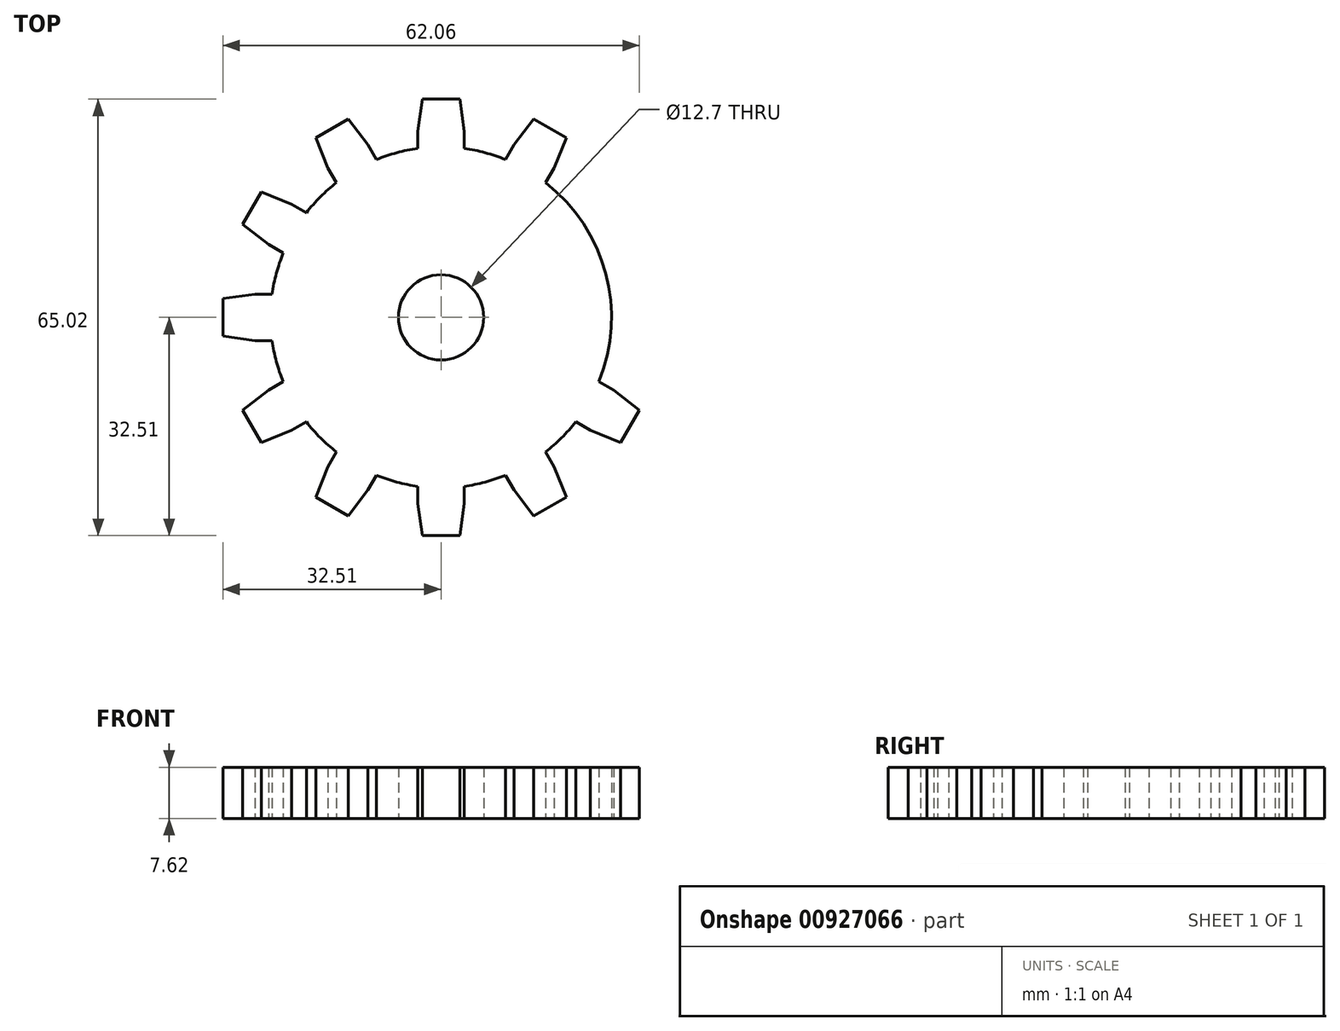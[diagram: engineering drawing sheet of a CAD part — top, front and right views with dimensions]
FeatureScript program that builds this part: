
annotation { "Feature Type Name" : "Feature", "Feature Type Description" : "" }
export const myFeature = defineFeature(function(context is Context, id is Id, definition is map)
    precondition{}
    {
        {
            var Q0;
            Q0=qCreatedBy(makeId("Top.planeOp"),FACE);
            var sketch = newSketch(context, id + "F0", { "sketchPlane" : qUnion([Q0])});
            skArc(sketch, "E0", {"start": v(-20.07, -15.57) * mm, "mid": v(-17.96, -17.96) * mm, "end": v(-15.57, -20.07) * mm});
            skLineSegment(sketch, "E1", {"start": v(0, 32.51) * mm, "end": v(2.8, 32.51) * mm});
            skLineSegment(sketch, "E2", {"start": v(2.8, 32.51) * mm, "end": v(3.45, 27.7) * mm});
            skLineSegment(sketch, "E3", {"start": v(3.45, 27.7) * mm, "end": v(3.45, 25.16) * mm});
            skLineSegment(sketch, "E4.MirrorCS", {"start": v(0, 32.51) * mm, "end": v(-2.8, 32.51) * mm});
            skLineSegment(sketch, "E5.MirrorCS", {"start": v(-2.8, 32.51) * mm, "end": v(-3.45, 27.7) * mm});
            skLineSegment(sketch, "E6.MirrorCS", {"start": v(-3.45, 27.7) * mm, "end": v(-3.45, 25.16) * mm});
            skLineSegment(sketch, "E7.1.0", {"start": v(-13.84, 29.55) * mm, "end": v(-10.87, 25.72) * mm});
            skLineSegment(sketch, "E7.1.1", {"start": v(-16.26, 28.16) * mm, "end": v(-13.84, 29.55) * mm});
            skLineSegment(sketch, "E7.1.2", {"start": v(-16.26, 28.16) * mm, "end": v(-18.68, 26.76) * mm});
            skLineSegment(sketch, "E7.1.3", {"start": v(-18.68, 26.76) * mm, "end": v(-16.84, 22.27) * mm});
            skLineSegment(sketch, "E7.1.4", {"start": v(-16.84, 22.27) * mm, "end": v(-15.57, 20.07) * mm});
            skLineSegment(sketch, "E7.1.5", {"start": v(-10.87, 25.72) * mm, "end": v(-9.6, 23.52) * mm});
            skLineSegment(sketch, "E7.2.0", {"start": v(-26.76, 18.68) * mm, "end": v(-22.27, 16.84) * mm});
            skLineSegment(sketch, "E7.2.1", {"start": v(-28.16, 16.26) * mm, "end": v(-26.76, 18.68) * mm});
            skLineSegment(sketch, "E7.2.2", {"start": v(-28.16, 16.26) * mm, "end": v(-29.55, 13.84) * mm});
            skLineSegment(sketch, "E7.2.3", {"start": v(-29.55, 13.84) * mm, "end": v(-25.72, 10.87) * mm});
            skLineSegment(sketch, "E7.2.4", {"start": v(-25.72, 10.87) * mm, "end": v(-23.52, 9.6) * mm});
            skLineSegment(sketch, "E7.2.5", {"start": v(-22.27, 16.84) * mm, "end": v(-20.07, 15.57) * mm});
            skLineSegment(sketch, "E7.3.0", {"start": v(-32.51, 2.8) * mm, "end": v(-27.7, 3.45) * mm});
            skLineSegment(sketch, "E7.3.1", {"start": v(-32.51, 0) * mm, "end": v(-32.51, 2.8) * mm});
            skLineSegment(sketch, "E7.3.2", {"start": v(-32.51, 0) * mm, "end": v(-32.51, -2.8) * mm});
            skLineSegment(sketch, "E7.3.3", {"start": v(-32.51, -2.8) * mm, "end": v(-27.7, -3.45) * mm});
            skLineSegment(sketch, "E7.3.4", {"start": v(-27.7, -3.45) * mm, "end": v(-25.16, -3.45) * mm});
            skLineSegment(sketch, "E7.3.5", {"start": v(-27.7, 3.45) * mm, "end": v(-25.16, 3.45) * mm});
            skLineSegment(sketch, "E7.4.0", {"start": v(-29.55, -13.84) * mm, "end": v(-25.72, -10.87) * mm});
            skLineSegment(sketch, "E7.4.1", {"start": v(-28.16, -16.26) * mm, "end": v(-29.55, -13.84) * mm});
            skLineSegment(sketch, "E7.4.2", {"start": v(-28.16, -16.26) * mm, "end": v(-26.76, -18.68) * mm});
            skLineSegment(sketch, "E7.4.3", {"start": v(-26.76, -18.68) * mm, "end": v(-22.27, -16.84) * mm});
            skLineSegment(sketch, "E7.4.4", {"start": v(-22.27, -16.84) * mm, "end": v(-20.07, -15.57) * mm});
            skLineSegment(sketch, "E7.4.5", {"start": v(-25.72, -10.87) * mm, "end": v(-23.52, -9.6) * mm});
            skLineSegment(sketch, "E7.5.0", {"start": v(-18.68, -26.76) * mm, "end": v(-16.84, -22.27) * mm});
            skLineSegment(sketch, "E7.5.1", {"start": v(-16.26, -28.16) * mm, "end": v(-18.68, -26.76) * mm});
            skLineSegment(sketch, "E7.5.2", {"start": v(-16.26, -28.16) * mm, "end": v(-13.84, -29.55) * mm});
            skLineSegment(sketch, "E7.5.3", {"start": v(-13.84, -29.55) * mm, "end": v(-10.87, -25.72) * mm});
            skLineSegment(sketch, "E7.5.4", {"start": v(-10.87, -25.72) * mm, "end": v(-9.6, -23.52) * mm});
            skLineSegment(sketch, "E7.5.5", {"start": v(-16.84, -22.27) * mm, "end": v(-15.57, -20.07) * mm});
            skLineSegment(sketch, "E7.6.0", {"start": v(-2.8, -32.51) * mm, "end": v(-3.45, -27.7) * mm});
            skLineSegment(sketch, "E7.6.1", {"start": v(0, -32.51) * mm, "end": v(-2.8, -32.51) * mm});
            skLineSegment(sketch, "E7.6.2", {"start": v(0, -32.51) * mm, "end": v(2.8, -32.51) * mm});
            skLineSegment(sketch, "E7.6.3", {"start": v(2.8, -32.51) * mm, "end": v(3.45, -27.7) * mm});
            skLineSegment(sketch, "E7.6.4", {"start": v(3.45, -27.7) * mm, "end": v(3.45, -25.16) * mm});
            skLineSegment(sketch, "E7.6.5", {"start": v(-3.45, -27.7) * mm, "end": v(-3.45, -25.16) * mm});
            skLineSegment(sketch, "E7.7.0", {"start": v(13.84, -29.55) * mm, "end": v(10.87, -25.72) * mm});
            skLineSegment(sketch, "E7.7.1", {"start": v(16.26, -28.16) * mm, "end": v(13.84, -29.55) * mm});
            skLineSegment(sketch, "E7.7.2", {"start": v(16.26, -28.16) * mm, "end": v(18.68, -26.76) * mm});
            skLineSegment(sketch, "E7.7.3", {"start": v(18.68, -26.76) * mm, "end": v(16.84, -22.27) * mm});
            skLineSegment(sketch, "E7.7.4", {"start": v(16.84, -22.27) * mm, "end": v(15.57, -20.07) * mm});
            skLineSegment(sketch, "E7.7.5", {"start": v(10.87, -25.72) * mm, "end": v(9.6, -23.52) * mm});
            skLineSegment(sketch, "E7.8.0", {"start": v(26.76, -18.68) * mm, "end": v(22.27, -16.84) * mm});
            skLineSegment(sketch, "E7.8.1", {"start": v(28.16, -16.26) * mm, "end": v(26.76, -18.68) * mm});
            skLineSegment(sketch, "E7.8.2", {"start": v(28.16, -16.26) * mm, "end": v(29.55, -13.84) * mm});
            skLineSegment(sketch, "E7.8.3", {"start": v(29.55, -13.84) * mm, "end": v(25.72, -10.87) * mm});
            skLineSegment(sketch, "E7.8.4", {"start": v(25.72, -10.87) * mm, "end": v(23.52, -9.6) * mm});
            skLineSegment(sketch, "E7.8.5", {"start": v(22.27, -16.84) * mm, "end": v(20.07, -15.57) * mm});
            skLineSegment(sketch, "E7.9.0", {"start": v(32.51, -2.8) * mm, "end": v(27.7, -3.45) * mm});
            skLineSegment(sketch, "E7.9.1", {"start": v(32.51, 0) * mm, "end": v(32.51, -2.8) * mm});
            skLineSegment(sketch, "E7.9.2", {"start": v(32.51, 0) * mm, "end": v(32.51, 2.8) * mm});
            skLineSegment(sketch, "E7.9.3", {"start": v(32.51, 2.8) * mm, "end": v(27.7, 3.45) * mm});
            skLineSegment(sketch, "E7.9.4", {"start": v(27.7, 3.45) * mm, "end": v(25.16, 3.45) * mm});
            skLineSegment(sketch, "E7.9.5", {"start": v(27.7, -3.45) * mm, "end": v(25.16, -3.45) * mm});
            skArc(sketch, "E8.trimOffspring", {"start": v(-25.16, -3.45) * mm, "mid": v(-24.53, -6.57) * mm, "end": v(-23.52, -9.6) * mm});
            skArc(sketch, "E9.trimOffspring", {"start": v(-23.52, 9.6) * mm, "mid": v(-24.53, 6.57) * mm, "end": v(-25.16, 3.45) * mm});
            skArc(sketch, "E10.trimOffspring", {"start": v(-15.57, 20.07) * mm, "mid": v(-17.96, 17.96) * mm, "end": v(-20.07, 15.57) * mm});
            skArc(sketch, "E11.trimOffspring", {"start": v(-3.45, 25.16) * mm, "mid": v(-6.57, 24.53) * mm, "end": v(-9.6, 23.52) * mm});
            skArc(sketch, "E12.trimOffspring", {"start": v(9.6, 23.52) * mm, "mid": v(6.57, 24.53) * mm, "end": v(3.45, 25.16) * mm});
            skArc(sketch, "E13.trimOffspring", {"start": v(23.52, -9.6) * mm, "mid": v(24.53, 6.57) * mm, "end": v(15.57, 20.07) * mm});
            skArc(sketch, "E14.trimOffspring", {"start": v(15.57, -20.07) * mm, "mid": v(17.96, -17.96) * mm, "end": v(20.07, -15.57) * mm});
            skArc(sketch, "E15.trimOffspring", {"start": v(3.45, -25.16) * mm, "mid": v(6.57, -24.53) * mm, "end": v(9.6, -23.52) * mm});
            skArc(sketch, "E16.trimOffspring", {"start": v(-9.6, -23.52) * mm, "mid": v(-6.57, -24.53) * mm, "end": v(-3.45, -25.16) * mm});
            skCircle(sketch, "E17", {"center": v(0, 0) * mm, "radius": 6.35 * mm});
            skLineSegment(sketch, "E18.2.10.0", {"start": v(29.55, 13.84) * mm, "end": v(25.72, 10.87) * mm});
            skLineSegment(sketch, "E18.3.10.0", {"start": v(28.16, 16.26) * mm, "end": v(29.55, 13.84) * mm});
            skLineSegment(sketch, "E18.6.10.0", {"start": v(28.16, 16.26) * mm, "end": v(26.76, 18.68) * mm});
            skLineSegment(sketch, "E18.9.10.0", {"start": v(26.76, 18.68) * mm, "end": v(22.27, 16.84) * mm});
            skLineSegment(sketch, "E18.12.10.0", {"start": v(22.27, 16.84) * mm, "end": v(20.07, 15.57) * mm});
            skLineSegment(sketch, "E18.15.10.0", {"start": v(25.72, 10.87) * mm, "end": v(23.52, 9.6) * mm});
            skLineSegment(sketch, "E18.2.11.0", {"start": v(18.68, 26.76) * mm, "end": v(16.84, 22.27) * mm});
            skLineSegment(sketch, "E18.3.11.0", {"start": v(16.26, 28.16) * mm, "end": v(18.68, 26.76) * mm});
            skLineSegment(sketch, "E18.6.11.0", {"start": v(16.26, 28.16) * mm, "end": v(13.84, 29.55) * mm});
            skLineSegment(sketch, "E18.9.11.0", {"start": v(13.84, 29.55) * mm, "end": v(10.87, 25.72) * mm});
            skLineSegment(sketch, "E18.12.11.0", {"start": v(10.87, 25.72) * mm, "end": v(9.6, 23.52) * mm});
            skLineSegment(sketch, "E18.15.11.0", {"start": v(16.84, 22.27) * mm, "end": v(15.57, 20.07) * mm});
            skSolve(sketch);
        }
        {
            var Q0;
            Q0=makeQuery(id+"F0.imprint","IMPRINT",FACE,{"disambiguationData":[TD([[makeQuery(id+"F0.imprint","IMPRINT",EDGE,{"derivedFrom":sQuery(id+"F0.wireOp",EDGE,"E0")}),1.0]])]});
            extrude(context, id + "F1", {"entities" : qUnion([Q0]), "endBound" : BoundingType.SYMMETRIC, "depth" : 7.62 * mm, "offsetDistance" : 25.4 * mm});
        }
    });
